# Revit family: v-754_904fr2_60Hz
name_source: partatom
category: 機械設備
units: mm (PartAtom-declared; Revit-internal decimal feet)

## family parameters
OmniClass タイトル = Centrifugal Fans
OmniClass 番号 = 23.75.35.17.27
パーツ タイプ = 標準
ロード時にボイドで切り取り = いいえ
丸型コネクタ寸法 = 直径を使用
作業面ベース = いいえ
共有 = いいえ
常に垂直 = はい
部屋計算ポイント = いいえ

## types (2) — shared parameters
D1 = 600
Depth = 340  [stored 1.11549 ft]
Duct_D = 125  [stored 0.410105 ft]
Duct_Height = 73
Duct_W = 30  [stored 0.0984252 ft]
EAサイズ_D = 148  [stored 0.485564 ft]
H1 = 55  [stored 0.180446 ft]
Height = 346  [stored 1.13517 ft]
IfcExportAs = IfcFanType
IfcExportType = CENTRIFUGALFORWARDCURVED
MAX静圧 = 0.0 Pa
MAX風量 = 490.0 m³/h
MID静圧 = 0.0 Pa
MID風量 = 300.0 m³/h
MIN静圧 = 0.0 Pa
MIN風量 = 130.0 m³/h
OmniClassCode = 23-33 31 19 13 15
URL = https://www.mitsubishielectric.co.jp
Uniclass2015Code = Pr_65_67_29_12
Uniclass2015Title = Centrifugal fans
Uniclass2015Version = Systems v1.9
Width = 557  [stored 1.82743 ft]
☑給気／□排気 = いいえ
ダクト径 = 150 mm
マテリアル = 鋼板(シルバー)
メンテナンススペース = はい
メンテナンススペース_高さ = 365
仕様書バージョン = Version1.0
企業コード = 108420
分類コード = 50052503100060
周波数 = 60 Hz
呼称 = 遠心送風機
外気量 = 0.0 m³/h
実風量 = 0.0 m³/h
形式 = 片吸込形
排気量 = 0.0 m³/h
極数 = 2
機外静圧 = 0.0 Pa
機外静圧_排気 = 210.0 Pa
法定耐用年数 = 15
消費電力 = 110 W
相 = 1
積算_科目 = 2 換気設備
符号 = FE
製品リリース年月 = 2022年6月1日
製品出荷対象 = 国内
製造元 = 三菱電機株式会社
設置方法 = 天吊
設計風量 = 0.0 m³/h
説明 = レンジフードファン フラット形
負荷分類 = 3_ファン類
運転質量 = 0.00 kg
電動機出力 = 0 W
電圧 = 100 V
風量 = 490.0 m³/h
騒音レベル(dB(A)) = 45
zero-valued in all types: Clearance Back, Clearance Bottom, Clearance Front, Clearance Left, Clearance Right, Clearance Top

## per-type parameters (varying)
| type | W1 | W2 | 価格 | 製品質量 | 質量 |
| V-754FR2 | 749  [stored 2.45735 ft] | 375 | 172500 $ | 28.00 kg | 33.60 kg |
| V-904FR2 | 899  [stored 2.94948 ft] | 450 | 197100 $ | 30.00 kg | 36.00 kg |

note: column(s) folded — value = type name in every type: モデル

note: [stored X ft] marks values corroborated as IEEE doubles in the binary element streams (Revit-internal decimal feet)

## geometry (parser evidence)
native form markers: Blend x2
no freeform markers — native parametric forms only
